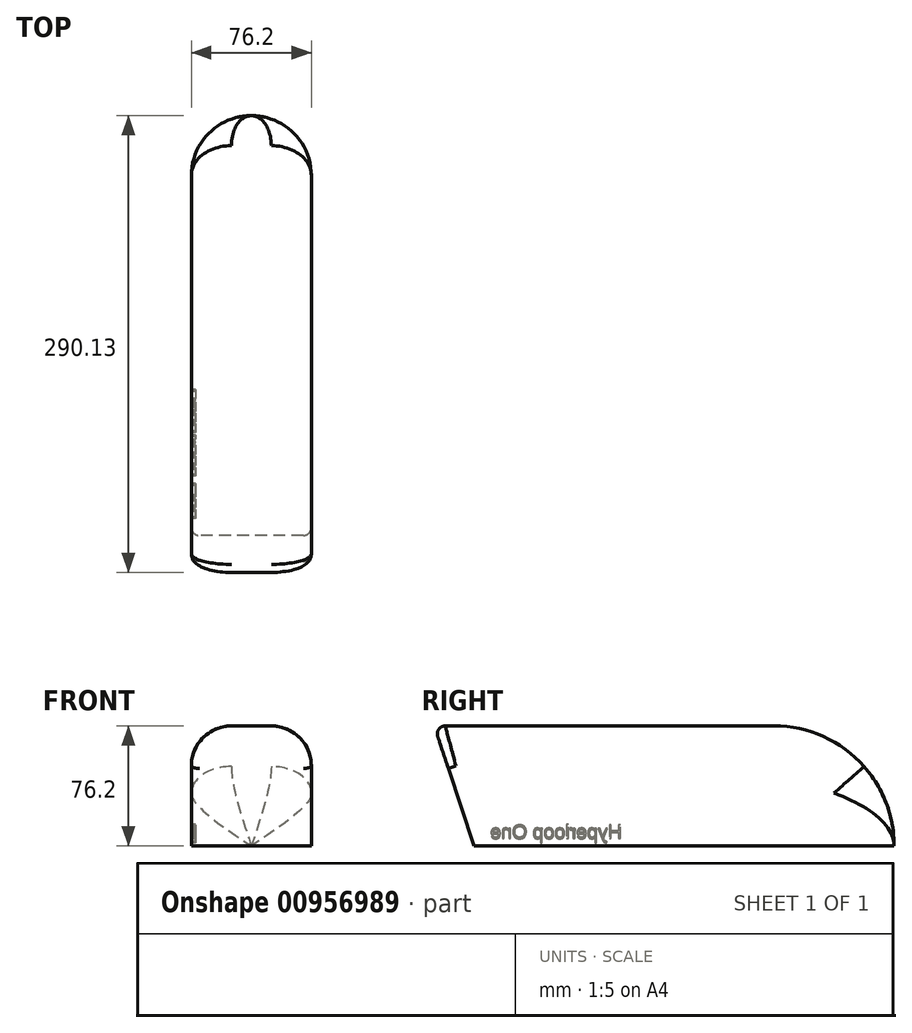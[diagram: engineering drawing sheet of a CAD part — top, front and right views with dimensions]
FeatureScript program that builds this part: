
annotation { "Feature Type Name" : "Feature", "Feature Type Description" : "" }
export const myFeature = defineFeature(function(context is Context, id is Id, definition is map)
    precondition{}
    {
        {
            var Q0;
            Q0=qCreatedBy(makeId("Top.planeOp"),FACE);
            var sketch = newSketch(context, id + "F0", { "sketchPlane" : qUnion([Q0])});
            skArc(sketch, "E0", {"start": v(0, 254) * mm, "mid": v(-38.1, 292.1) * mm, "end": v(-76.2, 254) * mm});
            skLineSegment(sketch, "E1", {"start": v(-76.2, 254) * mm, "end": v(-76.2, 0) * mm});
            skLineSegment(sketch, "E2", {"start": v(-76.2, 0) * mm, "end": v(0, 0) * mm});
            skLineSegment(sketch, "E3", {"start": v(0, 0) * mm, "end": v(0, 254) * mm});
            skSolve(sketch);
        }
        {
            var Q0;
            Q0 = qSketchRegion(id + "F0", true);
            extrude(context, id + "F1", {"entities" : qUnion([Q0]), "depth" : 76.2 * mm, "offsetDistance" : 25.4 * mm});
        }
        {
            var Q0;
            Q0=makeQuery(id+"F1.opExtrude","SWEPT_FACE",FACE,{"disambiguationData":[OSD([sQuery(id+"F0.wireOp",EDGE,"E1")])]});
            var sketch = newSketch(context, id + "F2", { "sketchPlane" : qUnion([Q0])});
            skPoint(sketch, "E4.endSnap0", {"position": v(-254, 38.1) * mm});
            skArc(sketch, "E5", {"start": v(-215.9, 76.2) * mm, "mid": v(-269.78, 53.88) * mm, "end": v(-292.1, 0) * mm});
            skLineSegment(sketch, "E6", {"start": v(-292.1, 0) * mm, "end": v(-254, 0) * mm});
            skLineSegment(sketch, "E7", {"start": v(-292.1, 0) * mm, "end": v(-292.1, 76.2) * mm});
            skLineSegment(sketch, "E8", {"start": v(-215.9, 76.2) * mm, "end": v(-292.1, 76.2) * mm});
            skSolve(sketch);
        }
        {
            var Q0;
            {var subQ0=sQuery(id+"F2.wireOp",EDGE,"E7");Q0=makeQuery(id+"F2.imprint","IMPRINT",FACE,{"disambiguationData":[TD([[makeQuery(id+"F2.imprint","IMPRINT",EDGE,{"derivedFrom":subQ0}),-1.0]])]});}
            var Q1;
            {var subQ0=sQuery(id+"F2.wireOp",EDGE,"E8");var subQ1=sQuery(id+"F2.wireOp",EDGE,"E5");var subQ2=sQuery(id+"F0.wireOp",EDGE,"E1");var subQ3=makeQuery(id+"F2.imprint","INTERSECT",VERTEX,{"derivedFrom":[makeQuery(id+"F1.opExtrude","CAP_EDGE",EDGE,{"disambiguationData":[OSD([subQ2])],"isStart":false}),subQ1,subQ0]});Q1=makeQuery(id+"F2.imprint","IMPRINT",FACE,{"disambiguationData":[TD([[makeQuery(id+"F2.imprint","IMPRINT",EDGE,{"disambiguationData":[TD([[subQ3,-1.0]])],"derivedFrom":subQ1}),-1.0]])]});}
            extrude(context, id + "F3", {"entities" : qUnion([Q0, Q1]), "operationType" : NewBodyOperationType.REMOVE, "endBound" : BoundingType.THROUGH_ALL, "oppositeDirection" : true, "depth" : 25.4 * mm, "offsetDistance" : 25.4 * mm});
        }
        {
            var Q0;
            Q0=makeQuery(id+"F3.boolean.opBoolean","INTERSECT",EDGE,{"disambiguationData":[OD(0.0)],"derivedFrom":[makeQuery(id+"F1.opExtrude","SWEPT_FACE",FACE,{"disambiguationData":[OSD([sQuery(id+"F0.wireOp",EDGE,"E0")])]}),makeQuery(id+"F3.opExtrude","SWEPT_FACE",FACE,{"disambiguationData":[OSD([sQuery(id+"F2.wireOp",EDGE,"E5")])]})]});
            var Q1;
            Q1=makeQuery(id+"F3.boolean.opBoolean","INTERSECT",EDGE,{"disambiguationData":[OD(1.0)],"derivedFrom":[makeQuery(id+"F1.opExtrude","SWEPT_FACE",FACE,{"disambiguationData":[OSD([sQuery(id+"F0.wireOp",EDGE,"E0")])]}),makeQuery(id+"F3.opExtrude","SWEPT_FACE",FACE,{"disambiguationData":[OSD([sQuery(id+"F2.wireOp",EDGE,"E5")])]})]});
            fillet(context, id + "F4", {"entities" : qUnion([Q0, Q1]), "radius" : 25.4 * mm, "tangentPropagation" : true, "allowEdgeOverflow" : false});
        }
        {
            var Q0;
            Q0=makeQuery(id+"F1.opExtrude","SWEPT_FACE",FACE,{"disambiguationData":[OSD([sQuery(id+"F0.wireOp",EDGE,"E1")])]});
            var sketch = newSketch(context, id + "F5", { "sketchPlane" : qUnion([Q0])});
            skLineSegment(sketch, "E9", {"start": v(-25.4, 0) * mm, "end": v(0, 76.2) * mm});
            skLineSegment(sketch, "E10", {"start": v(0, 76.2) * mm, "end": v(0, 0) * mm});
            skLineSegment(sketch, "E11", {"start": v(0, 0) * mm, "end": v(-25.4, 0) * mm});
            skSolve(sketch);
        }
        {
            var Q0;
            Q0 = qSketchRegion(id + "F5", true);
            extrude(context, id + "F6", {"entities" : qUnion([Q0]), "operationType" : NewBodyOperationType.REMOVE, "endBound" : BoundingType.THROUGH_ALL, "oppositeDirection" : true, "depth" : 25.4 * mm, "offsetDistance" : 25.4 * mm});
        }
        {
            var Q0;
            Q0=makeQuery(id+"F1.opExtrude","SWEPT_FACE",FACE,{"disambiguationData":[OSD([sQuery(id+"F0.wireOp",EDGE,"E1")])]});
            var sketch = newSketch(context, id + "F7", { "sketchPlane" : qUnion([Q0])});
            skText(sketch, "E12", { "text": "Hyperloop One", "fontName": "Arimo-Regular.ttf"});
            const initialGuessF7  = {"E12": [-0.1192, 0.00462, 1, 0, 0.00895]};
            skSetInitialGuess(sketch, initialGuessF7);
            skSolve(sketch);
        }
        {
            var Q0;
            Q0 = qSketchRegion(id + "F7", true);
            extrude(context, id + "F8", {"entities" : qUnion([Q0]), "operationType" : NewBodyOperationType.REMOVE, "oppositeDirection" : true, "depth" : 2.54 * mm, "offsetDistance" : 25.4 * mm});
        }
        {
            var Q0;
            Q0=makeQuery(id+"F6.boolean.opBoolean","INTERSECT",EDGE,{"derivedFrom":[makeQuery(id+"F4.opFillet","BLEND_FACE",FACE,{"disambiguationData":[OSD([sQuery(id+"F0.wireOp",EDGE,"E1")])]}),makeQuery(id+"F6.opExtrude","SWEPT_FACE",FACE,{"disambiguationData":[OSD([sQuery(id+"F5.wireOp",EDGE,"E9")])]})]});
            fillet(context, id + "F9", {"entities" : qUnion([Q0]), "radius" : 5.08 * mm, "tangentPropagation" : true, "allowEdgeOverflow" : false});
        }
    });
